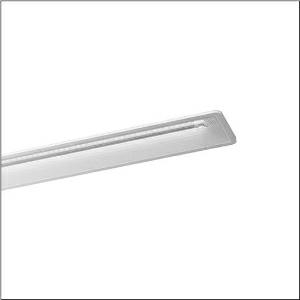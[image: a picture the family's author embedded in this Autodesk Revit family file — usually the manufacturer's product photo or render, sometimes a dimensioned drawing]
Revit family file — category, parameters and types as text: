
# Revit family: taris_r__21_5mt116d04wd_aa9a
name_source: partatom
category: Lighting Fixtures
units: mm (PartAtom-declared; Revit-internal decimal feet)

## family parameters
Cut with Voids When Loaded = No
Host = Face
Light Source = No
Part Type = Normal
Room Calculation Point = No
Round Connector Dimension = Use Diameter
Shared = No

## types (1)
- --- (1 x LED, 4910 lm, 28.9 W, 4000K)
    Apparent Load = 29 VA
    CIE Flux Codes = 73 96 99 100 100
    Color Rendering = 80
    Color Temperature = 4000K
    Default Elevation = 1800 mm
    Description = Taris® 21, office luminaire, primary anti-glare with micro louvre, primary optical cover: axial lens, of PMMA, structured, CAT 2 (L<= 1500cd/m²), light emission: direct distribution, primary light characteristic: symmetric, installation type: recessed, LED rated luminous flux: 4.910 lm, light colour: 840, colour temperature: 4000K, control gear: ECG DALI, with terminal, 5-pole, mains connection: 230V, AC, 50Hz, rated input power: 29W, housing, luminaire housing, of plastic, traffic white (RAL 9016), module: M625, length: 1.250 mm, width: 150 mm, height: 76mm, recess depth: 106 mm, protection rating (complete): IP20, insulation class (complete): insulation class I (protective earthing), certification: CE, ENEC, VDE, protection symbol: F, impact resistance: IK02, permissible ambient temperature for indoor applications: 0..+35°C, standard: EN 50419, packaging unit: 1 piece
    Height = 0 mm  [stored 0 ft]
    Lamp = 1 x LED
    Lamp Light Flux = 4910 lm
    Lamp Power = 28.9 W
    Lamp count = 1
    Length = 1243 mm
    Luminous efficacy = 170 lm/W
    Manufacturer = Siteco
    ModVariant = No
    Model = 5MT116D04WD
    Mounting Place = Ceiling
    Mounting Type = Recessed
    Number of Poles = 1
    OnlyDefault = Yes
    Power Factor = 1
    Product Name = Taris® 21
    Product group = office luminaire | ceiling recessed
    ProductGroupID = 400
    Protection Class = Protection class I
    Protection Degree = IP 20
    RLX_Detail_Level = 1
    RlxData = <blob elided: 30017 chars, md5=e57b0cf0>
    Socket = socket
    Standby Power = 0 W
    System Light Flux = 4910 lm
    System Power = 29 W
    Type Comments = factory setting: luminous flux: 100 % | dim-lin: 254 | 200 mA
    Type Image = l_1004723.jpg
    URL = http://relux.com
    VarID = @adj_130021
    Voltage = 0 V
    Weight = 0.00 kg
    Width = 144 mm

note: [stored X ft] marks values corroborated as IEEE doubles in the binary element streams (Revit-internal decimal feet)

## geometry (parser evidence)
native form markers: Blend x4, Sweep x10
no freeform markers — native parametric forms only
